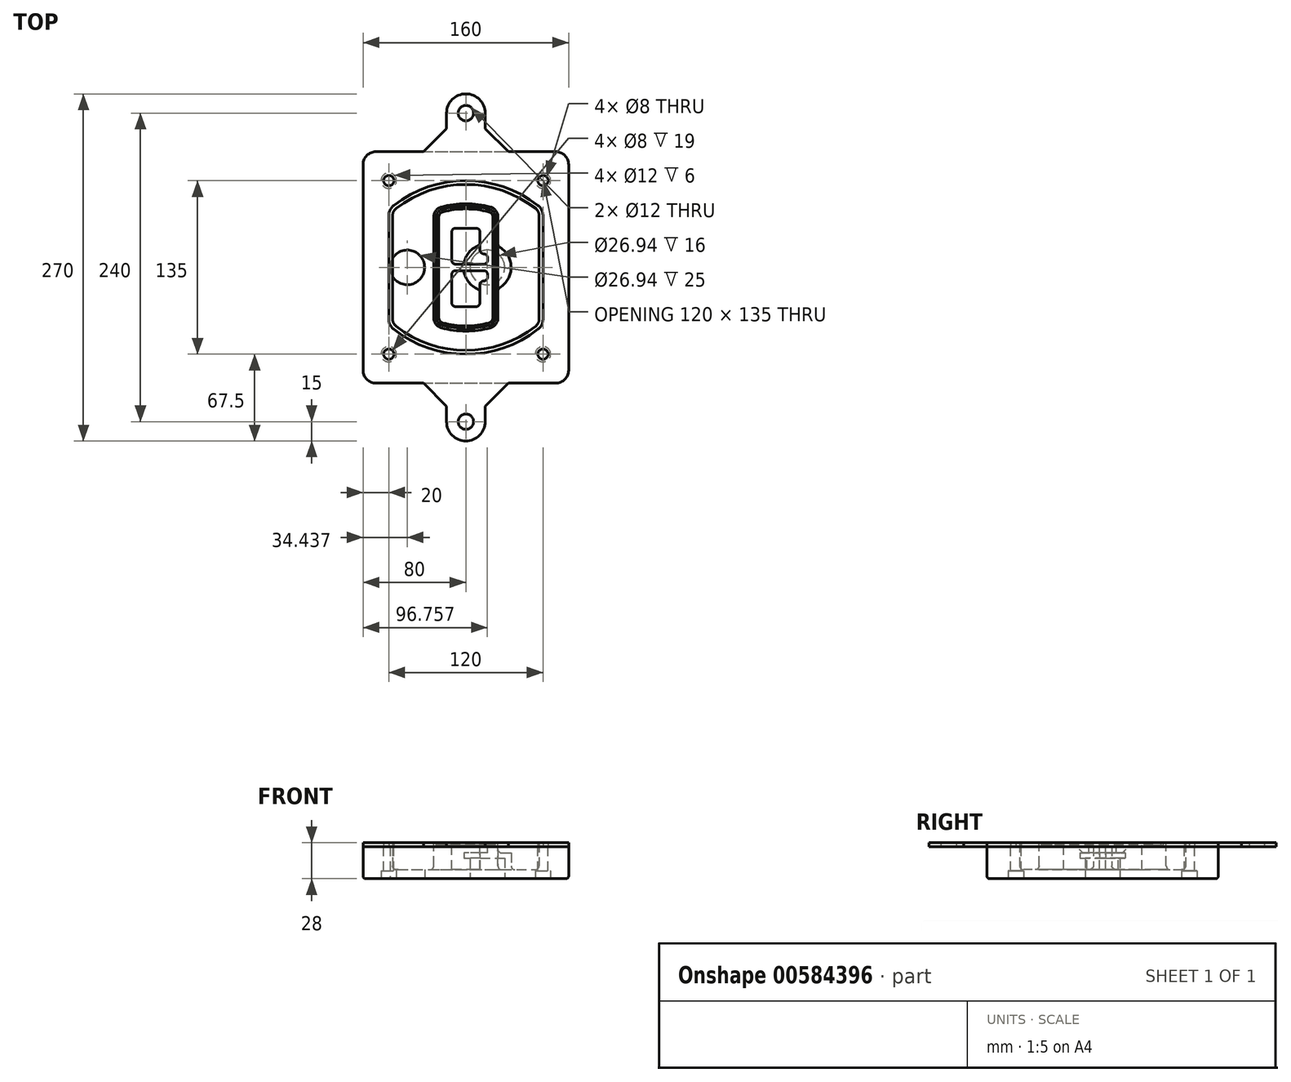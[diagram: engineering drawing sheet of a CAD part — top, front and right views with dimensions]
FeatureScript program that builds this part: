
annotation { "Feature Type Name" : "Feature", "Feature Type Description" : "" }
export const myFeature = defineFeature(function(context is Context, id is Id, definition is map)
    precondition{}
    {
        {
            var Q0;
            Q0=qCreatedBy(makeId("Top.planeOp"),FACE);
            var sketch = newSketch(context, id + "F0", { "sketchPlane" : qUnion([Q0])});
            skPoint(sketch, "E0.rect.middle", {"position": v(0, 0) * mm});
            skLineSegment(sketch, "E1.bottom", {"start": v(-70, -90) * mm, "end": v(70, -90) * mm});
            skLineSegment(sketch, "E1.top", {"start": v(-70, 90) * mm, "end": v(70, 90) * mm});
            skLineSegment(sketch, "E1.left", {"start": v(-80, -80) * mm, "end": v(-80, 80) * mm});
            skLineSegment(sketch, "E1.right", {"start": v(80, -80) * mm, "end": v(80, 80) * mm});
            skLineSegment(sketch, "E2", {"start": v(-80, 90) * mm, "end": v(80, -90) * mm, "construction": true});
            skLineSegment(sketch, "E3", {"start": v(80, 90) * mm, "end": v(-80, -90) * mm, "construction": true});
            skCircle(sketch, "E4", {"center": v(-60, 67.5) * mm, "radius": 4 * mm});
            skCircle(sketch, "E5", {"center": v(60, 67.5) * mm, "radius": 4 * mm});
            skCircle(sketch, "E6", {"center": v(60, -67.5) * mm, "radius": 4 * mm});
            skCircle(sketch, "E7", {"center": v(-60, -67.5) * mm, "radius": 4 * mm});
            skLineSegment(sketch, "E8", {"start": v(-60, 67.5) * mm, "end": v(60, 67.5) * mm, "construction": true});
            skLineSegment(sketch, "E9", {"start": v(60, 67.5) * mm, "end": v(60, -67.5) * mm, "construction": true});
            skLineSegment(sketch, "E10", {"start": v(60, -67.5) * mm, "end": v(-60, -67.5) * mm, "construction": true});
            skLineSegment(sketch, "E11", {"start": v(-60, -67.5) * mm, "end": v(-60, 67.5) * mm, "construction": true});
            skLineSegment(sketch, "E12", {"start": v(-60, 40.3) * mm, "end": v(-60, -40.3) * mm});
            skLineSegment(sketch, "E13", {"start": v(60, 40.3) * mm, "end": v(60, -40.3) * mm});
            skArc(sketch, "E14", {"start": v(56.15, 48.18) * mm, "mid": v(0, 67.5) * mm, "end": v(-56.15, 48.18) * mm});
            skArc(sketch, "E15", {"start": v(-56.15, -48.18) * mm, "mid": v(0, -67.5) * mm, "end": v(56.15, -48.18) * mm});
            skLineSegment(sketch, "E16", {"start": v(-60, 0) * mm, "end": v(60, 0) * mm, "construction": true});
            skPoint(sketch, "E17.visualSharp", {"position": v(-60, -45) * mm});
            skArc(sketch, "E17.filletArc", {"start": v(-60, -40.3) * mm, "mid": v(-58.99, -44.68) * mm, "end": v(-56.15, -48.18) * mm});
            skPoint(sketch, "E18.visualSharp", {"position": v(-60, 45) * mm});
            skArc(sketch, "E18.filletArc", {"start": v(-56.15, 48.18) * mm, "mid": v(-58.99, 44.68) * mm, "end": v(-60, 40.3) * mm});
            skPoint(sketch, "E19.visualSharp", {"position": v(60, 45) * mm});
            skArc(sketch, "E19.filletArc", {"start": v(60, 40.3) * mm, "mid": v(58.99, 44.68) * mm, "end": v(56.15, 48.18) * mm});
            skPoint(sketch, "E20.visualSharp", {"position": v(60, -45) * mm});
            skArc(sketch, "E20.filletArc", {"start": v(56.15, -48.18) * mm, "mid": v(58.99, -44.68) * mm, "end": v(60, -40.3) * mm});
            skPoint(sketch, "E21.visualSharp", {"position": v(-80, 90) * mm});
            skArc(sketch, "E21.filletArc", {"start": v(-70, 90) * mm, "mid": v(-77.07, 87.07) * mm, "end": v(-80, 80) * mm});
            skPoint(sketch, "E22.visualSharp", {"position": v(80, 90) * mm});
            skArc(sketch, "E22.filletArc", {"start": v(80, 80) * mm, "mid": v(77.07, 87.07) * mm, "end": v(70, 90) * mm});
            skPoint(sketch, "E23.visualSharp", {"position": v(80, -90) * mm});
            skArc(sketch, "E23.filletArc", {"start": v(70, -90) * mm, "mid": v(77.07, -87.07) * mm, "end": v(80, -80) * mm});
            skPoint(sketch, "E24.visualSharp", {"position": v(-80, -90) * mm});
            skArc(sketch, "E24.filletArc", {"start": v(-80, -80) * mm, "mid": v(-77.07, -87.07) * mm, "end": v(-70, -90) * mm});
            skArc(sketch, "E25.0", {"start": v(57, 40.3) * mm, "mid": v(56.3, 43.36) * mm, "end": v(54.3, 45.81) * mm});
            skLineSegment(sketch, "E25.1", {"start": v(57, 40.3) * mm, "end": v(57, -40.3) * mm});
            skArc(sketch, "E25.2", {"start": v(54.3, -45.81) * mm, "mid": v(56.3, -43.36) * mm, "end": v(57, -40.3) * mm});
            skArc(sketch, "E25.3", {"start": v(-54.3, -45.81) * mm, "mid": v(0, -64.5) * mm, "end": v(54.3, -45.81) * mm});
            skArc(sketch, "E25.4", {"start": v(-57, -40.3) * mm, "mid": v(-56.3, -43.36) * mm, "end": v(-54.3, -45.81) * mm});
            skArc(sketch, "E25.5", {"start": v(54.3, 45.81) * mm, "mid": v(0, 64.5) * mm, "end": v(-54.3, 45.81) * mm});
            skLineSegment(sketch, "E25.6", {"start": v(-57, 40.3) * mm, "end": v(-57, -40.3) * mm});
            skArc(sketch, "E25.7", {"start": v(-54.3, 45.81) * mm, "mid": v(-56.3, 43.36) * mm, "end": v(-57, 40.3) * mm});
            skArc(sketch, "E26.0", {"start": v(-58.62, 51.33) * mm, "mid": v(-62.58, 46.43) * mm, "end": v(-64, 40.3) * mm});
            skArc(sketch, "E26.1", {"start": v(58.62, 51.33) * mm, "mid": v(0, 71.5) * mm, "end": v(-58.62, 51.33) * mm});
            skArc(sketch, "E26.2", {"start": v(64, 40.3) * mm, "mid": v(62.58, 46.43) * mm, "end": v(58.62, 51.33) * mm});
            skLineSegment(sketch, "E26.3", {"start": v(64, 40.3) * mm, "end": v(64, -40.3) * mm});
            skArc(sketch, "E26.4", {"start": v(58.62, -51.33) * mm, "mid": v(62.58, -46.43) * mm, "end": v(64, -40.3) * mm});
            skLineSegment(sketch, "E26.5", {"start": v(-64, 40.3) * mm, "end": v(-64, -40.3) * mm});
            skArc(sketch, "E26.6", {"start": v(-58.62, -51.33) * mm, "mid": v(0, -71.5) * mm, "end": v(58.62, -51.33) * mm});
            skArc(sketch, "E26.7", {"start": v(-64, -40.3) * mm, "mid": v(-62.58, -46.43) * mm, "end": v(-58.62, -51.33) * mm});
            skSolve(sketch);
        }
        {
            var Q0;
            Q0=makeQuery(id+"F0.imprint","IMPRINT",FACE,{"disambiguationData":[TD([[makeQuery(id+"F0.imprint","IMPRINT",EDGE,{"derivedFrom":sQuery(id+"F0.wireOp",EDGE,"E1.bottom")}),1.0]])]});
            var Q1;
            Q1=makeQuery(id+"F0.imprint","IMPRINT",FACE,{"disambiguationData":[TD([[makeQuery(id+"F0.imprint","IMPRINT",EDGE,{"derivedFrom":sQuery(id+"F0.wireOp",EDGE,"E12")}),1.0]])]});
            var Q2;
            Q2=makeQuery(id+"F0.imprint","IMPRINT",FACE,{"disambiguationData":[TD([[makeQuery(id+"F0.imprint","IMPRINT",EDGE,{"derivedFrom":sQuery(id+"F0.wireOp",EDGE,"E25.0")}),1.0]])]});
            var Q3;
            Q3=makeQuery(id+"F0.imprint","IMPRINT",FACE,{"disambiguationData":[TD([[makeQuery(id+"F0.imprint","IMPRINT",EDGE,{"derivedFrom":sQuery(id+"F0.wireOp",EDGE,"E12")}),-1.0]])]});
            extrude(context, id + "F1", {"entities" : qUnion([Q0, Q1, Q2, Q3]), "oppositeDirection" : true, "depth" : 25 * mm});
        }
        {
            var Q0;
            Q0=makeQuery(id+"F0.imprint","IMPRINT",FACE,{"disambiguationData":[TD([[makeQuery(id+"F0.imprint","IMPRINT",EDGE,{"derivedFrom":sQuery(id+"F0.wireOp",EDGE,"E12")}),1.0]])]});
            extrude(context, id + "F2", {"entities" : qUnion([Q0]), "operationType" : NewBodyOperationType.ADD, "depth" : 3 * mm});
        }
        {
            var Q0;
            Q0=makeQuery(id+"F0.imprint","IMPRINT",FACE,{"disambiguationData":[TD([[makeQuery(id+"F0.imprint","IMPRINT",EDGE,{"derivedFrom":sQuery(id+"F0.wireOp",EDGE,"E25.0")}),1.0]])]});
            extrude(context, id + "F3", {"entities" : qUnion([Q0]), "operationType" : NewBodyOperationType.REMOVE, "oppositeDirection" : true, "depth" : 18 * mm});
        }
        {
            var Q0;
            Q0=makeQuery(id+"F2.opExtrude","CAP_FACE",FACE,{"disambiguationData":[OSD([sQuery(id+"F0.wireOp",EDGE,"E12"),sQuery(id+"F0.wireOp",EDGE,"E13"),sQuery(id+"F0.wireOp",EDGE,"E14"),sQuery(id+"F0.wireOp",EDGE,"E15"),sQuery(id+"F0.wireOp",EDGE,"E17.filletArc"),sQuery(id+"F0.wireOp",EDGE,"E18.filletArc"),sQuery(id+"F0.wireOp",EDGE,"E19.filletArc"),sQuery(id+"F0.wireOp",EDGE,"E20.filletArc"),sQuery(id+"F0.wireOp",EDGE,"E25.0"),sQuery(id+"F0.wireOp",EDGE,"E25.1"),sQuery(id+"F0.wireOp",EDGE,"E25.2"),sQuery(id+"F0.wireOp",EDGE,"E25.3"),sQuery(id+"F0.wireOp",EDGE,"E25.4"),sQuery(id+"F0.wireOp",EDGE,"E25.5"),sQuery(id+"F0.wireOp",EDGE,"E25.6"),sQuery(id+"F0.wireOp",EDGE,"E25.7")])],"isStart":false});
            var sketch = newSketch(context, id + "F4", { "sketchPlane" : qUnion([Q0])});
            skArc(sketch, "E27.0", {"start": v(-19.08, -46.97) * mm, "mid": v(0, -49.5) * mm, "end": v(19.08, -46.97) * mm});
            skArc(sketch, "E28.0", {"start": v(19.08, 46.97) * mm, "mid": v(0, 49.5) * mm, "end": v(-19.08, 46.97) * mm});
            skLineSegment(sketch, "E29", {"start": v(-25, 39.25) * mm, "end": v(-25, -39.25) * mm});
            skLineSegment(sketch, "E30", {"start": v(25, 39.25) * mm, "end": v(25, -39.25) * mm});
            skLineSegment(sketch, "E31", {"start": v(-25, 45.1) * mm, "end": v(25, 45.1) * mm, "construction": true});
            skLineSegment(sketch, "E32", {"start": v(-25, -45.1) * mm, "end": v(25, -45.1) * mm, "construction": true});
            skPoint(sketch, "E33.visualSharp", {"position": v(-25, 45.1) * mm});
            skArc(sketch, "E33.filletArc", {"start": v(-19.08, 46.97) * mm, "mid": v(-23.35, 44.11) * mm, "end": v(-25, 39.25) * mm});
            skPoint(sketch, "E34.visualSharp", {"position": v(25, 45.1) * mm});
            skArc(sketch, "E34.filletArc", {"start": v(25, 39.25) * mm, "mid": v(23.35, 44.11) * mm, "end": v(19.08, 46.97) * mm});
            skPoint(sketch, "E35.visualSharp", {"position": v(25, -45.1) * mm});
            skArc(sketch, "E35.filletArc", {"start": v(19.08, -46.97) * mm, "mid": v(23.35, -44.11) * mm, "end": v(25, -39.25) * mm});
            skPoint(sketch, "E36.visualSharp", {"position": v(-25, -45.1) * mm});
            skArc(sketch, "E36.filletArc", {"start": v(-25, -39.25) * mm, "mid": v(-23.35, -44.11) * mm, "end": v(-19.08, -46.97) * mm});
            skArc(sketch, "E37.0", {"start": v(54.3, 45.81) * mm, "mid": v(0, 64.5) * mm, "end": v(-54.3, 45.81) * mm});
            skArc(sketch, "E37.1", {"start": v(-54.3, 45.81) * mm, "mid": v(-56.3, 43.36) * mm, "end": v(-57, 40.3) * mm});
            skLineSegment(sketch, "E37.2", {"start": v(-57, 40.3) * mm, "end": v(-57, -40.3) * mm});
            skArc(sketch, "E37.3", {"start": v(-57, -40.3) * mm, "mid": v(-56.3, -43.36) * mm, "end": v(-54.3, -45.81) * mm});
            skArc(sketch, "E37.4", {"start": v(-54.3, -45.81) * mm, "mid": v(0, -64.5) * mm, "end": v(54.3, -45.81) * mm});
            skArc(sketch, "E37.5", {"start": v(54.3, -45.81) * mm, "mid": v(56.3, -43.36) * mm, "end": v(57, -40.3) * mm});
            skLineSegment(sketch, "E37.6", {"start": v(57, 40.3) * mm, "end": v(57, -40.3) * mm});
            skArc(sketch, "E37.7", {"start": v(57, 40.3) * mm, "mid": v(56.3, 43.36) * mm, "end": v(54.3, 45.81) * mm});
            skLineSegment(sketch, "E38.0", {"start": v(23, 39.25) * mm, "end": v(23, -39.25) * mm});
            skArc(sketch, "E38.1", {"start": v(18.56, -45.04) * mm, "mid": v(21.76, -42.9) * mm, "end": v(23, -39.25) * mm});
            skArc(sketch, "E38.2", {"start": v(-18.56, -45.04) * mm, "mid": v(0, -47.5) * mm, "end": v(18.56, -45.04) * mm});
            skArc(sketch, "E38.3", {"start": v(-23, -39.25) * mm, "mid": v(-21.76, -42.9) * mm, "end": v(-18.56, -45.04) * mm});
            skLineSegment(sketch, "E38.4", {"start": v(-23, 39.25) * mm, "end": v(-23, -39.25) * mm});
            skArc(sketch, "E38.5", {"start": v(23, 39.25) * mm, "mid": v(21.76, 42.9) * mm, "end": v(18.56, 45.04) * mm});
            skArc(sketch, "E38.6", {"start": v(-18.56, 45.04) * mm, "mid": v(-21.76, 42.9) * mm, "end": v(-23, 39.25) * mm});
            skArc(sketch, "E38.7", {"start": v(18.56, 45.04) * mm, "mid": v(0, 47.5) * mm, "end": v(-18.56, 45.04) * mm});
            skArc(sketch, "E39.0", {"start": v(21, 39.25) * mm, "mid": v(20.18, 41.68) * mm, "end": v(18.04, 43.1) * mm});
            skLineSegment(sketch, "E39.1", {"start": v(21, 39.25) * mm, "end": v(21, -39.25) * mm});
            skArc(sketch, "E39.2", {"start": v(18.04, -43.1) * mm, "mid": v(20.18, -41.68) * mm, "end": v(21, -39.25) * mm});
            skArc(sketch, "E39.3", {"start": v(-18.04, -43.1) * mm, "mid": v(0, -45.5) * mm, "end": v(18.04, -43.1) * mm});
            skArc(sketch, "E39.4", {"start": v(-21, -39.25) * mm, "mid": v(-20.18, -41.68) * mm, "end": v(-18.04, -43.1) * mm});
            skArc(sketch, "E39.5", {"start": v(18.04, 43.1) * mm, "mid": v(0, 45.5) * mm, "end": v(-18.04, 43.1) * mm});
            skLineSegment(sketch, "E39.6", {"start": v(-21, 39.25) * mm, "end": v(-21, -39.25) * mm});
            skArc(sketch, "E39.7", {"start": v(-18.04, 43.1) * mm, "mid": v(-20.18, 41.68) * mm, "end": v(-21, 39.25) * mm});
            skLineSegment(sketch, "E40", {"start": v(-25, 0) * mm, "end": v(25, 0) * mm, "construction": true});
            skLineSegment(sketch, "E41", {"start": v(-11, 5.5) * mm, "end": v(-11, 27.5) * mm});
            skLineSegment(sketch, "E42", {"start": v(-8, 30.5) * mm, "end": v(8, 30.5) * mm});
            skLineSegment(sketch, "E43", {"start": v(11, 27.5) * mm, "end": v(11, 13.5) * mm});
            skLineSegment(sketch, "E44", {"start": v(14, 10.5) * mm, "end": v(14, 10.5) * mm});
            skLineSegment(sketch, "E45", {"start": v(17, 7.5) * mm, "end": v(17, 5.5) * mm});
            skLineSegment(sketch, "E46", {"start": v(14, 2.5) * mm, "end": v(-8, 2.5) * mm});
            skPoint(sketch, "E47.visualSharp", {"position": v(-11, 30.5) * mm});
            skArc(sketch, "E47.filletArc", {"start": v(-8, 30.5) * mm, "mid": v(-10.12, 29.62) * mm, "end": v(-11, 27.5) * mm});
            skPoint(sketch, "E48.visualSharp", {"position": v(11, 30.5) * mm});
            skArc(sketch, "E48.filletArc", {"start": v(11, 27.5) * mm, "mid": v(10.12, 29.62) * mm, "end": v(8, 30.5) * mm});
            skPoint(sketch, "E49.visualSharp", {"position": v(11, 10.5) * mm});
            skArc(sketch, "E49.filletArc", {"start": v(11, 13.5) * mm, "mid": v(11.88, 11.38) * mm, "end": v(14, 10.5) * mm});
            skPoint(sketch, "E50.visualSharp", {"position": v(17, 10.5) * mm});
            skArc(sketch, "E50.filletArc", {"start": v(17, 7.5) * mm, "mid": v(16.12, 9.62) * mm, "end": v(14, 10.5) * mm});
            skPoint(sketch, "E51.visualSharp", {"position": v(17, 2.5) * mm});
            skArc(sketch, "E51.filletArc", {"start": v(14, 2.5) * mm, "mid": v(16.12, 3.38) * mm, "end": v(17, 5.5) * mm});
            skPoint(sketch, "E52.visualSharp", {"position": v(-11, 2.5) * mm});
            skArc(sketch, "E52.filletArc", {"start": v(-11, 5.5) * mm, "mid": v(-10.12, 3.38) * mm, "end": v(-8, 2.5) * mm});
            skLineSegment(sketch, "E53.0.MirrorCS", {"start": v(14, -2.5) * mm, "end": v(-8, -2.5) * mm});
            skArc(sketch, "E54.0.MirrorCS", {"start": v(-11, -5.5) * mm, "mid": v(-10.12, -3.38) * mm, "end": v(-8, -2.5) * mm});
            skLineSegment(sketch, "E55.0.MirrorCS", {"start": v(-11, -5.5) * mm, "end": v(-11, -27.5) * mm});
            skArc(sketch, "E56.0.MirrorCS", {"start": v(-8, -30.5) * mm, "mid": v(-10.12, -29.62) * mm, "end": v(-11, -27.5) * mm});
            skLineSegment(sketch, "E57.0.MirrorCS", {"start": v(-8, -30.5) * mm, "end": v(8, -30.5) * mm});
            skArc(sketch, "E58.0.MirrorCS", {"start": v(11, -27.5) * mm, "mid": v(10.12, -29.62) * mm, "end": v(8, -30.5) * mm});
            skLineSegment(sketch, "E59.0.MirrorCS", {"start": v(11, -27.5) * mm, "end": v(11, -13.5) * mm});
            skArc(sketch, "E60.0.MirrorCS", {"start": v(11, -13.5) * mm, "mid": v(11.88, -11.38) * mm, "end": v(14, -10.5) * mm});
            skArc(sketch, "E61.0.MirrorCS", {"start": v(17, -7.5) * mm, "mid": v(16.12, -9.62) * mm, "end": v(14, -10.5) * mm});
            skLineSegment(sketch, "E62.0.MirrorCS", {"start": v(17, -7.5) * mm, "end": v(17, -5.5) * mm});
            skArc(sketch, "E63.0.MirrorCS", {"start": v(14, -2.5) * mm, "mid": v(16.12, -3.38) * mm, "end": v(17, -5.5) * mm});
            skSolve(sketch);
        }
        {
            var Q0;
            Q0=makeQuery(id+"F4.imprint","IMPRINT",FACE,{"disambiguationData":[TD([[makeQuery(id+"F4.imprint","IMPRINT",EDGE,{"derivedFrom":sQuery(id+"F4.wireOp",EDGE,"E27.0")}),1.0]])]});
            var Q1;
            Q1=makeQuery(id+"F4.imprint","IMPRINT",FACE,{"disambiguationData":[TD([[makeQuery(id+"F4.imprint","IMPRINT",EDGE,{"derivedFrom":sQuery(id+"F4.wireOp",EDGE,"E38.0")}),-1.0]])]});
            var Q2;
            Q2=makeQuery(id+"F4.imprint","IMPRINT",FACE,{"disambiguationData":[TD([[makeQuery(id+"F4.imprint","IMPRINT",EDGE,{"derivedFrom":sQuery(id+"F4.wireOp",EDGE,"E39.0")}),1.0]])]});
            extrude(context, id + "F5", {"entities" : qUnion([Q0, Q1, Q2]), "operationType" : NewBodyOperationType.ADD, "endBound" : BoundingType.UP_TO_NEXT, "oppositeDirection" : true, "depth" : 25 * mm});
        }
        {
            var Q0;
            Q0=makeQuery(id+"F4.imprint","IMPRINT",FACE,{"disambiguationData":[TD([[makeQuery(id+"F4.imprint","IMPRINT",EDGE,{"derivedFrom":sQuery(id+"F4.wireOp",EDGE,"E38.0")}),-1.0]])]});
            extrude(context, id + "F6", {"entities" : qUnion([Q0]), "operationType" : NewBodyOperationType.REMOVE, "oppositeDirection" : true, "depth" : 2 * mm});
        }
        {
            var Q0;
            Q0=makeQuery(id+"F1.opExtrude","CAP_FACE",FACE,{"disambiguationData":[OSD([sQuery(id+"F0.wireOp",EDGE,"E1.bottom"),sQuery(id+"F0.wireOp",EDGE,"E1.top"),sQuery(id+"F0.wireOp",EDGE,"E1.left"),sQuery(id+"F0.wireOp",EDGE,"E1.right"),sQuery(id+"F0.wireOp",EDGE,"E4"),sQuery(id+"F0.wireOp",EDGE,"E5"),sQuery(id+"F0.wireOp",EDGE,"E6"),sQuery(id+"F0.wireOp",EDGE,"E7"),sQuery(id+"F0.wireOp",EDGE,"E21.filletArc"),sQuery(id+"F0.wireOp",EDGE,"E22.filletArc"),sQuery(id+"F0.wireOp",EDGE,"E23.filletArc"),sQuery(id+"F0.wireOp",EDGE,"E24.filletArc")])],"isStart":false});
            var sketch = newSketch(context, id + "F7", { "sketchPlane" : qUnion([Q0])});
            skCircle(sketch, "E64", {"center": v(16.76, 0) * mm, "radius": 13.47 * mm});
            skCircle(sketch, "E65", {"center": v(-45.56, 0) * mm, "radius": 13.47 * mm});
            skLineSegment(sketch, "E66", {"start": v(80, 0) * mm, "end": v(-80, 0) * mm});
            skCircle(sketch, "E67", {"center": v(16.76, 0) * mm, "radius": 18.47 * mm});
            skCircle(sketch, "E68", {"center": v(60, -67.5) * mm, "radius": 6 * mm});
            skCircle(sketch, "E69", {"center": v(-60, -67.5) * mm, "radius": 6 * mm});
            skCircle(sketch, "E70", {"center": v(-60, 67.5) * mm, "radius": 6 * mm});
            skCircle(sketch, "E71", {"center": v(60, 67.5) * mm, "radius": 6 * mm});
            skSolve(sketch);
        }
        {
            var Q0;
            {var subQ1=sQuery(id+"F7.wireOp",EDGE,"E66");var subQ4=sQuery(id+"F7.wireOp",EDGE,"E64");var subQ6=makeQuery(id+"F7.imprint","INTERSECT",VERTEX,{"disambiguationData":[OD(0.0)],"derivedFrom":[subQ4,subQ1]});Q0=makeQuery(id+"F7.imprint","IMPRINT",FACE,{"disambiguationData":[TD([[makeQuery(id+"F7.imprint","IMPRINT",EDGE,{"disambiguationData":[TD([[subQ6,-1.0]])],"derivedFrom":subQ4}),-1.0]])]});}
            var Q1;
            {var subQ0=sQuery(id+"F7.wireOp",EDGE,"E66");var subQ1=sQuery(id+"F7.wireOp",EDGE,"E64");var subQ3=makeQuery(id+"F7.imprint","INTERSECT",VERTEX,{"disambiguationData":[OD(0.0)],"derivedFrom":[subQ1,subQ0]});Q1=makeQuery(id+"F7.imprint","IMPRINT",FACE,{"disambiguationData":[TD([[makeQuery(id+"F7.imprint","IMPRINT",EDGE,{"disambiguationData":[TD([[subQ3,-1.0]])],"derivedFrom":subQ1}),1.0]])]});}
            var Q2;
            {var subQ0=sQuery(id+"F7.wireOp",EDGE,"E66");var subQ1=sQuery(id+"F7.wireOp",EDGE,"E64");var subQ3=makeQuery(id+"F7.imprint","INTERSECT",VERTEX,{"disambiguationData":[OD(0.0)],"derivedFrom":[subQ1,subQ0]});Q2=makeQuery(id+"F7.imprint","IMPRINT",FACE,{"disambiguationData":[TD([[makeQuery(id+"F7.imprint","IMPRINT",EDGE,{"disambiguationData":[TD([[subQ3,1.0]])],"derivedFrom":subQ1}),1.0]])]});}
            var Q3;
            {var subQ1=sQuery(id+"F7.wireOp",EDGE,"E66");var subQ4=sQuery(id+"F7.wireOp",EDGE,"E64");var subQ6=makeQuery(id+"F7.imprint","INTERSECT",VERTEX,{"disambiguationData":[OD(0.0)],"derivedFrom":[subQ4,subQ1]});Q3=makeQuery(id+"F7.imprint","IMPRINT",FACE,{"disambiguationData":[TD([[makeQuery(id+"F7.imprint","IMPRINT",EDGE,{"disambiguationData":[TD([[subQ6,1.0]])],"derivedFrom":subQ4}),-1.0]])]});}
            extrude(context, id + "F8", {"entities" : qUnion([Q0, Q1, Q2, Q3]), "operationType" : NewBodyOperationType.ADD, "oppositeDirection" : true, "depth" : 20 * mm});
        }
        {
            var Q0;
            {var subQ0=sQuery(id+"F7.wireOp",EDGE,"E66");var subQ1=sQuery(id+"F7.wireOp",EDGE,"E64");var subQ3=makeQuery(id+"F7.imprint","INTERSECT",VERTEX,{"disambiguationData":[OD(0.0)],"derivedFrom":[subQ1,subQ0]});Q0=makeQuery(id+"F7.imprint","IMPRINT",FACE,{"disambiguationData":[TD([[makeQuery(id+"F7.imprint","IMPRINT",EDGE,{"disambiguationData":[TD([[subQ3,-1.0]])],"derivedFrom":subQ1}),1.0]])]});}
            var Q1;
            {var subQ0=sQuery(id+"F7.wireOp",EDGE,"E66");var subQ1=sQuery(id+"F7.wireOp",EDGE,"E64");var subQ3=makeQuery(id+"F7.imprint","INTERSECT",VERTEX,{"disambiguationData":[OD(0.0)],"derivedFrom":[subQ1,subQ0]});Q1=makeQuery(id+"F7.imprint","IMPRINT",FACE,{"disambiguationData":[TD([[makeQuery(id+"F7.imprint","IMPRINT",EDGE,{"disambiguationData":[TD([[subQ3,1.0]])],"derivedFrom":subQ1}),1.0]])]});}
            extrude(context, id + "F9", {"entities" : qUnion([Q0, Q1]), "operationType" : NewBodyOperationType.REMOVE, "oppositeDirection" : true, "depth" : 16 * mm});
        }
        {
            var Q0;
            {var subQ0=sQuery(id+"F7.wireOp",EDGE,"E66");var subQ1=sQuery(id+"F7.wireOp",EDGE,"E65");var subQ3=makeQuery(id+"F7.imprint","INTERSECT",VERTEX,{"disambiguationData":[OD(0.0)],"derivedFrom":[subQ1,subQ0]});Q0=makeQuery(id+"F7.imprint","IMPRINT",FACE,{"disambiguationData":[TD([[makeQuery(id+"F7.imprint","IMPRINT",EDGE,{"disambiguationData":[TD([[subQ3,-1.0]])],"derivedFrom":subQ1}),1.0]])]});}
            var Q1;
            {var subQ0=sQuery(id+"F7.wireOp",EDGE,"E66");var subQ1=sQuery(id+"F7.wireOp",EDGE,"E65");var subQ3=makeQuery(id+"F7.imprint","INTERSECT",VERTEX,{"disambiguationData":[OD(0.0)],"derivedFrom":[subQ1,subQ0]});Q1=makeQuery(id+"F7.imprint","IMPRINT",FACE,{"disambiguationData":[TD([[makeQuery(id+"F7.imprint","IMPRINT",EDGE,{"disambiguationData":[TD([[subQ3,1.0]])],"derivedFrom":subQ1}),1.0]])]});}
            extrude(context, id + "F10", {"entities" : qUnion([Q0, Q1]), "operationType" : NewBodyOperationType.REMOVE, "oppositeDirection" : true, "depth" : 25 * mm});
        }
        {
            var Q0;
            Q0=makeQuery(id+"F7.imprint","IMPRINT",FACE,{"disambiguationData":[TD([[makeQuery(id+"F7.imprint","IMPRINT",EDGE,{"derivedFrom":sQuery(id+"F7.wireOp",EDGE,"E68")}),1.0]])]});
            var Q1;
            Q1=makeQuery(id+"F7.imprint","IMPRINT",FACE,{"disambiguationData":[TD([[makeQuery(id+"F7.imprint","IMPRINT",EDGE,{"derivedFrom":makeQuery(id+"F1.opExtrude","CAP_EDGE",EDGE,{"disambiguationData":[OSD([sQuery(id+"F0.wireOp",EDGE,"E5")])],"isStart":false})}),-1.0]])]});
            var Q2;
            Q2=makeQuery(id+"F7.imprint","IMPRINT",FACE,{"disambiguationData":[TD([[makeQuery(id+"F7.imprint","IMPRINT",EDGE,{"derivedFrom":sQuery(id+"F7.wireOp",EDGE,"E69")}),1.0]])]});
            var Q3;
            Q3=makeQuery(id+"F7.imprint","IMPRINT",FACE,{"disambiguationData":[TD([[makeQuery(id+"F7.imprint","IMPRINT",EDGE,{"derivedFrom":makeQuery(id+"F1.opExtrude","CAP_EDGE",EDGE,{"disambiguationData":[OSD([sQuery(id+"F0.wireOp",EDGE,"E4")])],"isStart":false})}),-1.0]])]});
            var Q4;
            Q4=makeQuery(id+"F7.imprint","IMPRINT",FACE,{"disambiguationData":[TD([[makeQuery(id+"F7.imprint","IMPRINT",EDGE,{"derivedFrom":sQuery(id+"F7.wireOp",EDGE,"E70")}),1.0]])]});
            var Q5;
            Q5=makeQuery(id+"F7.imprint","IMPRINT",FACE,{"disambiguationData":[TD([[makeQuery(id+"F7.imprint","IMPRINT",EDGE,{"derivedFrom":makeQuery(id+"F1.opExtrude","CAP_EDGE",EDGE,{"disambiguationData":[OSD([sQuery(id+"F0.wireOp",EDGE,"E7")])],"isStart":false})}),-1.0]])]});
            var Q6;
            Q6=makeQuery(id+"F7.imprint","IMPRINT",FACE,{"disambiguationData":[TD([[makeQuery(id+"F7.imprint","IMPRINT",EDGE,{"derivedFrom":sQuery(id+"F7.wireOp",EDGE,"E71")}),1.0]])]});
            var Q7;
            Q7=makeQuery(id+"F7.imprint","IMPRINT",FACE,{"disambiguationData":[TD([[makeQuery(id+"F7.imprint","IMPRINT",EDGE,{"derivedFrom":makeQuery(id+"F1.opExtrude","CAP_EDGE",EDGE,{"disambiguationData":[OSD([sQuery(id+"F0.wireOp",EDGE,"E6")])],"isStart":false})}),-1.0]])]});
            extrude(context, id + "F11", {"entities" : qUnion([Q0, Q1, Q2, Q3, Q4, Q5, Q6, Q7]), "operationType" : NewBodyOperationType.REMOVE, "oppositeDirection" : true, "depth" : 6 * mm});
        }
        {
            var Q0;
            Q0=makeQuery(id+"F9.boolean.opBoolean","COPY",FACE,{"derivedFrom":makeQuery(id+"F9.opExtrude","CAP_FACE",FACE,{"disambiguationData":[OSD([sQuery(id+"F7.wireOp",EDGE,"E64")])],"isStart":false})});
            var sketch = newSketch(context, id + "F12", { "sketchPlane" : qUnion([Q0])});
            skArc(sketch, "E72.0", {"start": v(11, 17.55) * mm, "mid": v(2.57, 11.82) * mm, "end": v(-1.54, 2.5) * mm});
            skArc(sketch, "E72.1", {"start": v(-1.54, -2.5) * mm, "mid": v(2.57, -11.82) * mm, "end": v(11, -17.55) * mm});
            skLineSegment(sketch, "E73", {"start": v(-1.54, -2.5) * mm, "end": v(14, -2.5) * mm});
            skLineSegment(sketch, "E74.0", {"start": v(14, 2.5) * mm, "end": v(-1.54, 2.5) * mm});
            skArc(sketch, "E74.1", {"start": v(14, 2.5) * mm, "mid": v(16.12, 3.38) * mm, "end": v(17, 5.5) * mm});
            skLineSegment(sketch, "E74.2", {"start": v(17, 7.5) * mm, "end": v(17, 5.5) * mm});
            skArc(sketch, "E74.3", {"start": v(17, 7.5) * mm, "mid": v(16.12, 9.62) * mm, "end": v(14, 10.5) * mm});
            skArc(sketch, "E74.4", {"start": v(11, 13.5) * mm, "mid": v(11.88, 11.38) * mm, "end": v(14, 10.5) * mm});
            skLineSegment(sketch, "E74.5", {"start": v(11, 17.55) * mm, "end": v(11, 13.5) * mm});
            skLineSegment(sketch, "E74.7", {"start": v(14, -2.5) * mm, "end": v(-1.54, -2.5) * mm});
            skArc(sketch, "E74.8", {"start": v(14, -2.5) * mm, "mid": v(16.12, -3.38) * mm, "end": v(17, -5.5) * mm});
            skLineSegment(sketch, "E74.9", {"start": v(17, -7.5) * mm, "end": v(17, -5.5) * mm});
            skArc(sketch, "E74.10", {"start": v(17, -7.5) * mm, "mid": v(16.12, -9.62) * mm, "end": v(14, -10.5) * mm});
            skArc(sketch, "E74.11", {"start": v(11, -13.5) * mm, "mid": v(11.88, -11.38) * mm, "end": v(14, -10.5) * mm});
            skLineSegment(sketch, "E74.12", {"start": v(11, -17.55) * mm, "end": v(11, -13.5) * mm});
            skPoint(sketch, "E75.orphan", {"position": v(11, -27.5) * mm});
            skPoint(sketch, "E76.orphan", {"position": v(-8, -2.5) * mm});
            skPoint(sketch, "E77.orphan", {"position": v(-8, 2.5) * mm});
            skPoint(sketch, "E78.orphan", {"position": v(11, 27.5) * mm});
            skSolve(sketch);
        }
        {
            var Q0;
            {var subQ7=sQuery(id+"F12.wireOp",EDGE,"E72.0");var subQ14=sQuery(id+"F12.wireOp",EDGE,"E72.1");var subQ16=sQuery(id+"F12.wireOp",EDGE,"E74.1");var subQ18=sQuery(id+"F12.wireOp",EDGE,"E74.8");Q0=qUnion([makeQuery(id+"F12.imprint","IMPRINT",FACE,{"disambiguationData":[TD([[makeQuery(id+"F12.imprint","IMPRINT",EDGE,{"derivedFrom":subQ7}),1.0]])]}),makeQuery(id+"F12.imprint","IMPRINT",FACE,{"disambiguationData":[TD([[makeQuery(id+"F12.imprint","IMPRINT",EDGE,{"derivedFrom":subQ14}),1.0]])]}),makeQuery(id+"F12.imprint","IMPRINT",FACE,{"disambiguationData":[TD([[makeQuery(id+"F12.imprint","IMPRINT",EDGE,{"derivedFrom":subQ16}),1.0]])]}),makeQuery(id+"F12.imprint","IMPRINT",FACE,{"disambiguationData":[TD([[makeQuery(id+"F12.imprint","IMPRINT",EDGE,{"derivedFrom":subQ18}),-1.0]])]})]);}
            var Q1;
            Q1=makeQuery(id+"F5.boolean.opBoolean","SPLIT",FACE,{"disambiguationData":[TD([makeQuery(id+"F5.opExtrude","SWEPT_FACE",FACE,{"disambiguationData":[OSD([sQuery(id+"F4.wireOp",EDGE,"E41")])]})])],"derivedFrom":makeQuery(id+"F3.boolean.opBoolean","COPY",FACE,{"derivedFrom":makeQuery(id+"F3.opExtrude","CAP_FACE",FACE,{"disambiguationData":[OSD([sQuery(id+"F0.wireOp",EDGE,"E25.0"),sQuery(id+"F0.wireOp",EDGE,"E25.1"),sQuery(id+"F0.wireOp",EDGE,"E25.2"),sQuery(id+"F0.wireOp",EDGE,"E25.3"),sQuery(id+"F0.wireOp",EDGE,"E25.4"),sQuery(id+"F0.wireOp",EDGE,"E25.5"),sQuery(id+"F0.wireOp",EDGE,"E25.6"),sQuery(id+"F0.wireOp",EDGE,"E25.7")])],"isStart":false})})});
            extrude(context, id + "F13", {"entities" : qUnion([Q0]), "operationType" : NewBodyOperationType.REMOVE, "endBound" : BoundingType.UP_TO_SURFACE, "endBoundEntityFace" : qUnion([Q1]), "depth" : 25 * mm});
        }
        {
            var Q0;
            Q0=makeQuery(id+"F3.boolean.opBoolean","COPY",EDGE,{"derivedFrom":makeQuery(id+"F3.opExtrude","CAP_EDGE",EDGE,{"disambiguationData":[OSD([sQuery(id+"F0.wireOp",EDGE,"E25.6")])],"isStart":false})});
            var Q1;
            Q1=makeQuery(id+"F8.boolean.opBoolean","INTERSECT",EDGE,{"derivedFrom":[makeQuery(id+"F5.opExtrude","SWEPT_FACE",FACE,{"disambiguationData":[OSD([sQuery(id+"F4.wireOp",EDGE,"E30")])]}),makeQuery(id+"F8.opExtrude","CAP_FACE",FACE,{"disambiguationData":[OSD([sQuery(id+"F7.wireOp",EDGE,"E67")])],"isStart":false})]});
            var Q2;
            Q2=makeQuery(id+"F8.boolean.opBoolean","INTERSECT",EDGE,{"disambiguationData":[OD(1.0)],"derivedFrom":[makeQuery(id+"F5.opExtrude","SWEPT_FACE",FACE,{"disambiguationData":[OSD([sQuery(id+"F4.wireOp",EDGE,"E30")])]}),makeQuery(id+"F8.opExtrude","SWEPT_FACE",FACE,{"disambiguationData":[OSD([sQuery(id+"F7.wireOp",EDGE,"E67")])]})]});
            var Q3;
            {var subQ0=sQuery(id+"F4.wireOp",EDGE,"E30");Q3=makeQuery(id+"F8.boolean.opBoolean","SPLIT",EDGE,{"disambiguationData":[TD([makeQuery(id+"F5.opExtrude","SWEPT_FACE",FACE,{"disambiguationData":[OSD([sQuery(id+"F4.wireOp",EDGE,"E35.filletArc")])]})])],"derivedFrom":makeQuery(id+"F5.opExtrude","CAP_EDGE",EDGE,{"disambiguationData":[OSD([subQ0])],"isStart":false})});}
            var Q4;
            {var subQ0=sQuery(id+"F0.wireOp",EDGE,"E25.7");var subQ1=sQuery(id+"F0.wireOp",EDGE,"E25.1");var subQ2=sQuery(id+"F0.wireOp",EDGE,"E25.6");var subQ3=sQuery(id+"F0.wireOp",EDGE,"E25.5");var subQ4=sQuery(id+"F0.wireOp",EDGE,"E25.4");var subQ5=sQuery(id+"F0.wireOp",EDGE,"E25.0");var subQ6=sQuery(id+"F0.wireOp",EDGE,"E25.2");var subQ7=sQuery(id+"F0.wireOp",EDGE,"E25.3");Q4=makeQuery(id+"F8.boolean.opBoolean","INTERSECT",EDGE,{"derivedFrom":[makeQuery(id+"F5.boolean.opBoolean","SPLIT",FACE,{"disambiguationData":[TD([makeQuery(id+"F2.opExtrude","SWEPT_FACE",FACE,{"disambiguationData":[OSD([subQ5])]})])],"derivedFrom":makeQuery(id+"F3.boolean.opBoolean","COPY",FACE,{"derivedFrom":makeQuery(id+"F3.opExtrude","CAP_FACE",FACE,{"disambiguationData":[OSD([subQ5,subQ1,subQ6,subQ7,subQ4,subQ3,subQ2,subQ0])],"isStart":false})})}),makeQuery(id+"F8.opExtrude","SWEPT_FACE",FACE,{"disambiguationData":[OSD([sQuery(id+"F7.wireOp",EDGE,"E67")])]})]});}
            var Q5;
            Q5=makeQuery(id+"F8.boolean.opBoolean","INTERSECT",EDGE,{"disambiguationData":[OD(0.0)],"derivedFrom":[makeQuery(id+"F5.opExtrude","SWEPT_FACE",FACE,{"disambiguationData":[OSD([sQuery(id+"F4.wireOp",EDGE,"E30")])]}),makeQuery(id+"F8.opExtrude","SWEPT_FACE",FACE,{"disambiguationData":[OSD([sQuery(id+"F7.wireOp",EDGE,"E67")])]})]});
            fillet(context, id + "F14", {"entities" : qUnion([Q0, Q1, Q2, Q3, Q4, Q5]), "radius" : 3 * mm, "tangentPropagation" : true, "allowEdgeOverflow" : false});
        }
        {
            var Q0;
            Q0=makeQuery(id+"F1.opExtrude","CAP_EDGE",EDGE,{"disambiguationData":[OSD([sQuery(id+"F0.wireOp",EDGE,"E1.bottom")])],"isStart":false});
            fillet(context, id + "F15", {"entities" : qUnion([Q0]), "radius" : 2 * mm, "tangentPropagation" : true, "allowEdgeOverflow" : false});
        }
        {
            var Q0;
            {var subQ0=sQuery(id+"F0.wireOp",EDGE,"E21.filletArc");var subQ1=sQuery(id+"F0.wireOp",EDGE,"E7");var subQ2=sQuery(id+"F0.wireOp",EDGE,"E6");var subQ3=sQuery(id+"F0.wireOp",EDGE,"E5");var subQ4=sQuery(id+"F0.wireOp",EDGE,"E4");var subQ5=sQuery(id+"F0.wireOp",EDGE,"E22.filletArc");var subQ6=sQuery(id+"F0.wireOp",EDGE,"E1.bottom");var subQ7=sQuery(id+"F0.wireOp",EDGE,"E1.right");var subQ8=sQuery(id+"F0.wireOp",EDGE,"E1.top");var subQ9=sQuery(id+"F0.wireOp",EDGE,"E1.left");var subQ10=sQuery(id+"F0.wireOp",EDGE,"E23.filletArc");var subQ11=sQuery(id+"F0.wireOp",EDGE,"E24.filletArc");Q0=makeQuery(id+"F2.boolean.opBoolean","SPLIT",FACE,{"disambiguationData":[TD([makeQuery(id+"F1.opExtrude","SWEPT_FACE",FACE,{"disambiguationData":[OSD([subQ6])]})])],"derivedFrom":makeQuery(id+"F1.opExtrude","CAP_FACE",FACE,{"disambiguationData":[OSD([subQ6,subQ8,subQ9,subQ7,subQ4,subQ3,subQ2,subQ1,subQ0,subQ5,subQ10,subQ11])],"isStart":true})});}
            var sketch = newSketch(context, id + "F16", { "sketchPlane" : qUnion([Q0])});
            skLineSegment(sketch, "E79", {"start": v(0, 90) * mm, "end": v(0, 120) * mm});
            skCircle(sketch, "E80", {"center": v(0, 120) * mm, "radius": 6 * mm});
            skArc(sketch, "E81", {"start": v(15, 120) * mm, "mid": v(0, 135) * mm, "end": v(-15, 120) * mm});
            skLineSegment(sketch, "E82", {"start": v(-15, 120) * mm, "end": v(-15, 108) * mm});
            skLineSegment(sketch, "E83", {"start": v(15, 120) * mm, "end": v(15, 108) * mm});
            skLineSegment(sketch, "E84", {"start": v(15, 108) * mm, "end": v(33, 90) * mm});
            skLineSegment(sketch, "E85", {"start": v(-15, 108) * mm, "end": v(-33, 90) * mm});
            skLineSegment(sketch, "E86", {"start": v(-80, 0) * mm, "end": v(80, 0) * mm});
            skLineSegment(sketch, "E87.MirrorCS", {"start": v(15, -120) * mm, "end": v(15, -108) * mm});
            skCircle(sketch, "E88.MirrorC", {"center": v(0, -120) * mm, "radius": 6 * mm});
            skArc(sketch, "E89.MirrorCS", {"start": v(15, -120) * mm, "mid": v(0, -135) * mm, "end": v(-15, -120) * mm});
            skLineSegment(sketch, "E90.MirrorCS", {"start": v(-15, -120) * mm, "end": v(-15, -108) * mm});
            skLineSegment(sketch, "E91.MirrorCS", {"start": v(-15, -108) * mm, "end": v(-33, -90) * mm});
            skLineSegment(sketch, "E92.MirrorCS", {"start": v(15, -108) * mm, "end": v(33, -90) * mm});
            skLineSegment(sketch, "E93.MirrorCS", {"start": v(0, -90) * mm, "end": v(0, -120) * mm});
            skSolve(sketch);
        }
        {
            var Q0;
            Q0 = qSketchRegion(id + "F16", true);
            var Q1;
            Q1=makeQuery(id+"F16.imprint","IMPRINT",FACE,{"disambiguationData":[TD([[makeQuery(id+"F16.imprint","IMPRINT",EDGE,{"derivedFrom":sQuery(id+"F16.wireOp",EDGE,"E80")}),-1.0]])]});
            var Q2;
            Q2=makeQuery(id+"F16.imprint","IMPRINT",FACE,{"disambiguationData":[TD([[makeQuery(id+"F16.imprint","IMPRINT",EDGE,{"derivedFrom":makeQuery(id+"F1.opExtrude","CAP_EDGE",EDGE,{"disambiguationData":[OSD([sQuery(id+"F0.wireOp",EDGE,"E4")])],"isStart":true})}),-1.0]])]});
            var Q3;
            Q3=makeQuery(id+"F16.imprint","IMPRINT",FACE,{"disambiguationData":[TD([[makeQuery(id+"F16.imprint","IMPRINT",EDGE,{"derivedFrom":makeQuery(id+"F1.opExtrude","CAP_EDGE",EDGE,{"disambiguationData":[OSD([sQuery(id+"F0.wireOp",EDGE,"E6")])],"isStart":true})}),-1.0]])]});
            var Q4;
            Q4=makeQuery(id+"F16.imprint","IMPRINT",FACE,{"disambiguationData":[TD([[makeQuery(id+"F16.imprint","IMPRINT",EDGE,{"derivedFrom":sQuery(id+"F16.wireOp",EDGE,"E87.MirrorCS")}),1.0]])]});
            var Q5;
            Q5=makeQuery(id+"F2.opExtrude","CAP_FACE",FACE,{"disambiguationData":[OSD([sQuery(id+"F0.wireOp",EDGE,"E12"),sQuery(id+"F0.wireOp",EDGE,"E13"),sQuery(id+"F0.wireOp",EDGE,"E14"),sQuery(id+"F0.wireOp",EDGE,"E15"),sQuery(id+"F0.wireOp",EDGE,"E17.filletArc"),sQuery(id+"F0.wireOp",EDGE,"E18.filletArc"),sQuery(id+"F0.wireOp",EDGE,"E19.filletArc"),sQuery(id+"F0.wireOp",EDGE,"E20.filletArc"),sQuery(id+"F0.wireOp",EDGE,"E25.0"),sQuery(id+"F0.wireOp",EDGE,"E25.1"),sQuery(id+"F0.wireOp",EDGE,"E25.2"),sQuery(id+"F0.wireOp",EDGE,"E25.3"),sQuery(id+"F0.wireOp",EDGE,"E25.4"),sQuery(id+"F0.wireOp",EDGE,"E25.5"),sQuery(id+"F0.wireOp",EDGE,"E25.6"),sQuery(id+"F0.wireOp",EDGE,"E25.7")])],"isStart":false});
            extrude(context, id + "F17", {"entities" : qUnion([Q0, Q1, Q2, Q3, Q4]), "endBound" : BoundingType.UP_TO_SURFACE, "depth" : 25 * mm, "endBoundEntityFace" : qUnion([Q5]), "offsetDistance" : 25 * mm});
        }
        {
            var Q0;
            Q0=sQuery(id+"F16.wireOp",VERTEX,"E80.center");
            var Q1;
            Q1=sQuery(id+"F16.wireOp",VERTEX,"E93.MirrorCS.end");
            var Q2;
            Q2=makeQuery(id+"F17.opExtrude","SWEPT_BODY",BODY,{"disambiguationData":[OSD([sQuery(id+"F0.wireOp",EDGE,"E1.bottom"),sQuery(id+"F0.wireOp",EDGE,"E1.top"),sQuery(id+"F0.wireOp",EDGE,"E1.left"),sQuery(id+"F0.wireOp",EDGE,"E1.right"),sQuery(id+"F0.wireOp",EDGE,"E4"),sQuery(id+"F0.wireOp",EDGE,"E5"),sQuery(id+"F0.wireOp",EDGE,"E6"),sQuery(id+"F0.wireOp",EDGE,"E7"),sQuery(id+"F0.wireOp",EDGE,"E12"),sQuery(id+"F0.wireOp",EDGE,"E13"),sQuery(id+"F0.wireOp",EDGE,"E14"),sQuery(id+"F0.wireOp",EDGE,"E15"),sQuery(id+"F0.wireOp",EDGE,"E17.filletArc"),sQuery(id+"F0.wireOp",EDGE,"E18.filletArc"),sQuery(id+"F0.wireOp",EDGE,"E19.filletArc"),sQuery(id+"F0.wireOp",EDGE,"E20.filletArc"),sQuery(id+"F0.wireOp",EDGE,"E21.filletArc"),sQuery(id+"F0.wireOp",EDGE,"E22.filletArc"),sQuery(id+"F0.wireOp",EDGE,"E23.filletArc"),sQuery(id+"F0.wireOp",EDGE,"E24.filletArc"),sQuery(id+"F16.wireOp",EDGE,"E81"),sQuery(id+"F16.wireOp",EDGE,"E82"),sQuery(id+"F16.wireOp",EDGE,"E83"),sQuery(id+"F16.wireOp",EDGE,"E84"),sQuery(id+"F16.wireOp",EDGE,"E85"),sQuery(id+"F16.wireOp",EDGE,"E87.MirrorCS"),sQuery(id+"F16.wireOp",EDGE,"E89.MirrorCS"),sQuery(id+"F16.wireOp",EDGE,"E90.MirrorCS"),sQuery(id+"F16.wireOp",EDGE,"E91.MirrorCS"),sQuery(id+"F16.wireOp",EDGE,"E92.MirrorCS")])]});
            hole(context, id + "F18", {"style" : HoleStyle.SIMPLE, "endStyle" : HoleEndStyle.THROUGH, "oppositeDirection" : true, "holeDiameter" : 12 * mm, "majorDiameter" : 5 * mm, "isTappedThrough" : true, "tappedDepth" : 12 * mm, "tapClearance" : 3, "locations" : qUnion([Q0, Q1]), "scope" : qUnion([Q2])});
        }
    });
